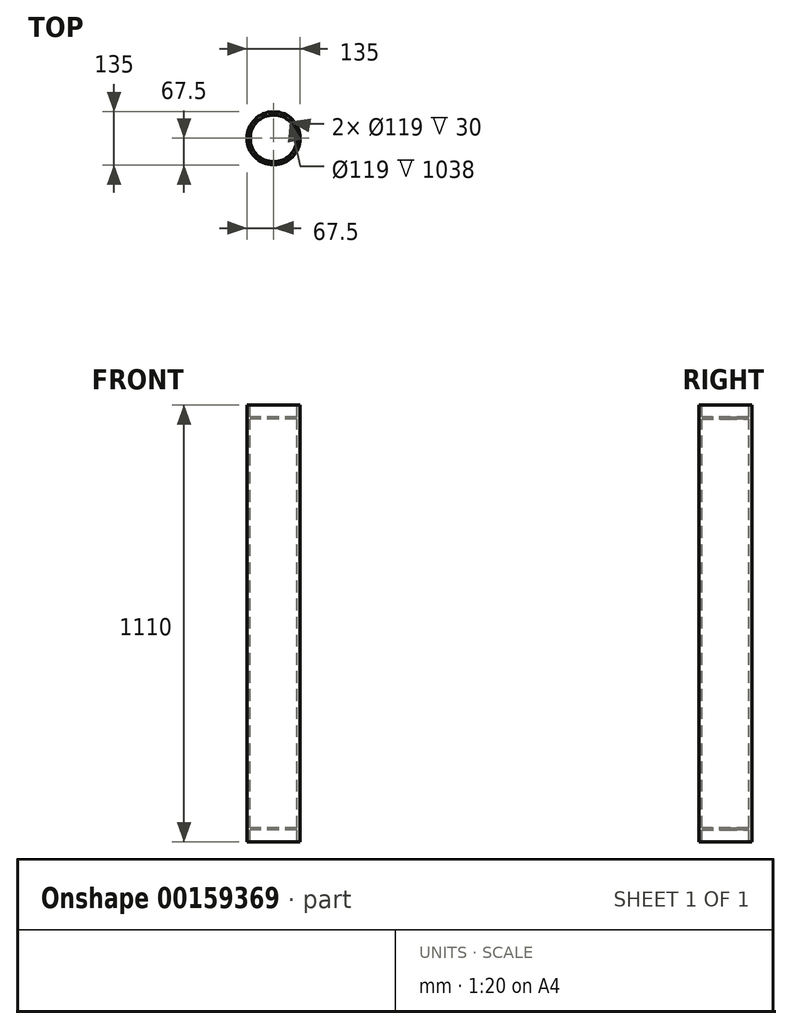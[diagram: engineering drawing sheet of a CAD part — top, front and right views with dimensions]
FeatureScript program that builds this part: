
annotation { "Feature Type Name" : "Feature", "Feature Type Description" : "" }
export const myFeature = defineFeature(function(context is Context, id is Id, definition is map)
    precondition{}
    {
        {
            var Q0;
            Q0=qCreatedBy(makeId("Front.planeOp"),FACE);
            var sketch = newSketch(context, id + "F0", { "sketchPlane" : qUnion([Q0])});
            skLineSegment(sketch, "E0", {"start": v(0, 672.07) * mm, "end": v(0, -680.1) * mm, "construction": true});
            skLineSegment(sketch, "E1", {"start": v(67.5, 555) * mm, "end": v(67.5, -555) * mm});
            skLineSegment(sketch, "E2", {"start": v(59.5, 555) * mm, "end": v(59.5, 525) * mm});
            skLineSegment(sketch, "E3", {"start": v(59.5, 555) * mm, "end": v(67.5, 555) * mm});
            skLineSegment(sketch, "E4.0", {"start": v(0, 525) * mm, "end": v(59.5, 525) * mm});
            skLineSegment(sketch, "E5", {"start": v(67.5, -555) * mm, "end": v(59.5, -555) * mm});
            skLineSegment(sketch, "E6.0", {"start": v(59.5, -525) * mm, "end": v(0, -525) * mm});
            skLineSegment(sketch, "E7.0", {"start": v(0, 519) * mm, "end": v(59.5, 519) * mm});
            skLineSegment(sketch, "E8.0", {"start": v(59.5, -519) * mm, "end": v(0, -519) * mm});
            skLineSegment(sketch, "E9.trimOffspring", {"start": v(59.5, -525) * mm, "end": v(59.5, -555) * mm});
            skPoint(sketch, "E10.orphan", {"position": v(0, 555) * mm});
            skLineSegment(sketch, "E11.trimOffspring", {"start": v(59.5, 519) * mm, "end": v(59.5, -519) * mm});
            skLineSegment(sketch, "E12", {"start": v(0, 525) * mm, "end": v(0, 519) * mm});
            skLineSegment(sketch, "E13", {"start": v(0, -519) * mm, "end": v(0, -525) * mm});
            skSolve(sketch);
        }
        {
            var Q0;
            Q0=makeQuery(id+"F0.imprint","IMPRINT",FACE,{"disambiguationData":[TD([[makeQuery(id+"F0.imprint","IMPRINT",EDGE,{"derivedFrom":sQuery(id+"F0.wireOp",EDGE,"E1")}),-1.0]])]});
            var Q1;
            Q1=sQuery(id+"F0.wireOp",EDGE,"E0");
            revolve(context, id + "F1", {"entities" : qUnion([Q0]), "axis" : qUnion([Q1]), "revolveType" : RevolveType.FULL});
        }
    });
